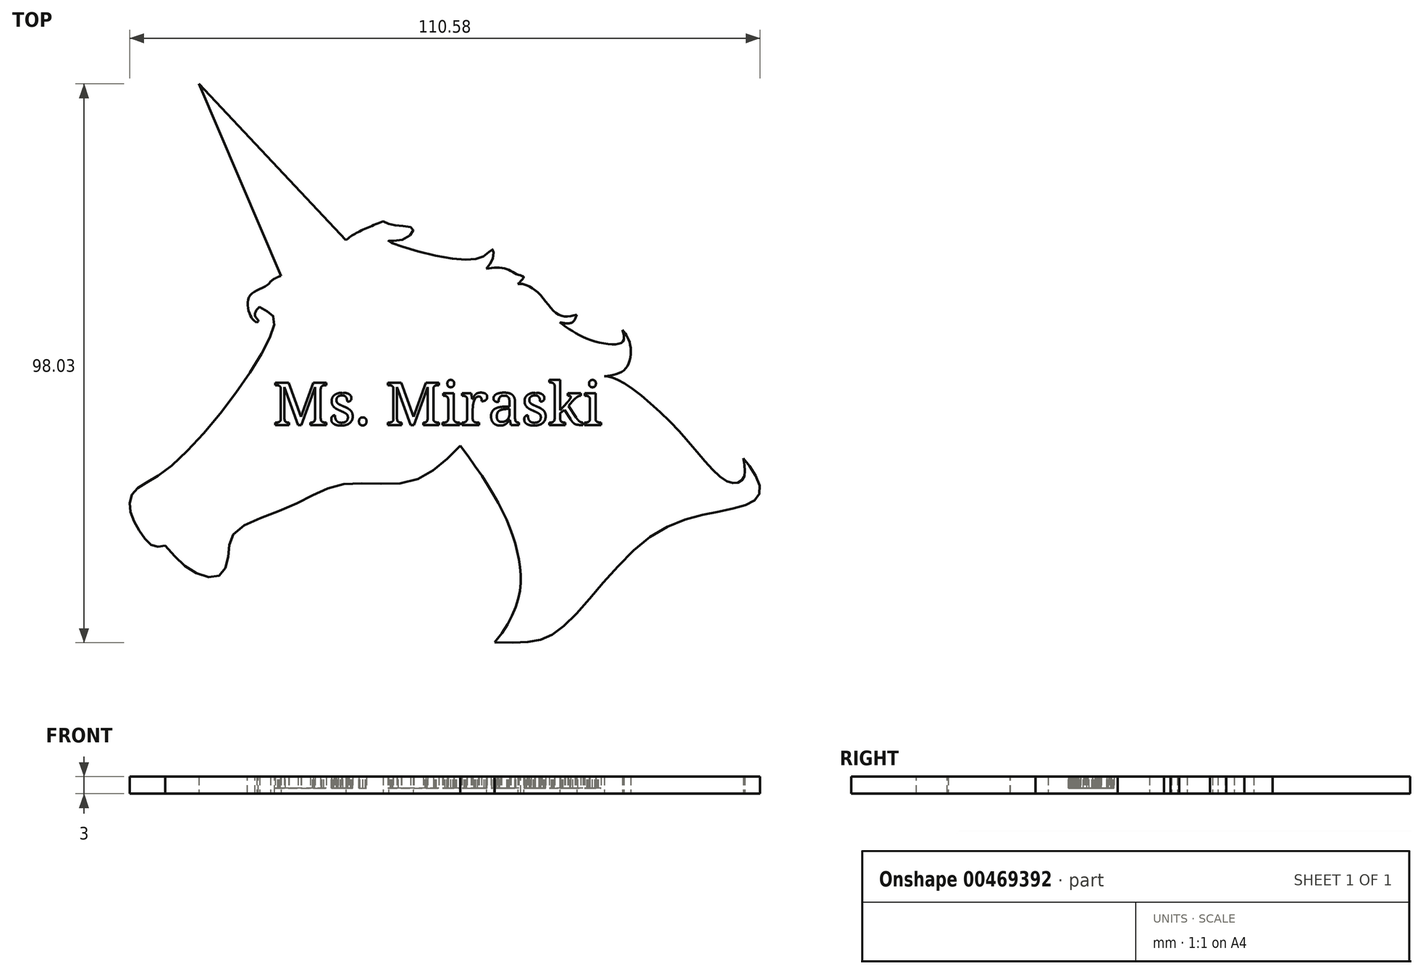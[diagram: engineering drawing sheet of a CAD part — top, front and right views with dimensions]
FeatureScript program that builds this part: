
annotation { "Feature Type Name" : "Feature", "Feature Type Description" : "" }
export const myFeature = defineFeature(function(context is Context, id is Id, definition is map)
    precondition{}
    {
        {
            var Q0;
            Q0=qCreatedBy(makeId("Top.planeOp"),FACE);
            var sketch = newSketch(context, id + "F0", { "sketchPlane" : qUnion([Q0])});
            skFitSpline(sketch, "E0", {"points": [v(22.82, -62.48) * mm, v(26.88, -47) * mm, v(16.78, -27.97) * mm], "startDerivative": vector(31.27, 37.7) * mm, "endDerivative": vector(-32.74, 43.32) * mm});
            skFitSpline(sketch, "E1", {"points": [v(16.78, -27.97) * mm, v(8.01, -34.25) * mm, v(-3.9, -34.75) * mm, v(-12.84, -38.56) * mm, v(-22.77, -43.2) * mm, v(-23.93, -47.5) * mm, v(-25.58, -50.8) * mm, v(-30.22, -49.98) * mm, v(-35, -45.51) * mm], "startDerivative": vector(-52.72, -53.92) * mm, "endDerivative": vector(-37.54, 43.37) * mm});
            skFitSpline(sketch, "E2", {"points": [v(-35, -45.51) * mm, v(-37.15, -45.51) * mm, v(-39.5, -42.86) * mm, v(-41.18, -38.88) * mm, v(-40.37, -35.9) * mm, v(-35, -32.4) * mm, v(-19.32, -13.9) * mm, v(-16.02, -5.26) * mm, v(-18.41, -3.62) * mm], "startDerivative": vector(-29.2, -5.84) * mm, "endDerivative": vector(-28.5, 26.2) * mm});
            skFitSpline(sketch, "E3", {"points": [v(-18.41, -3.62) * mm, v(-19.15, -5.35) * mm, v(-18.9, -6.38) * mm], "startDerivative": vector(-2.67, -1.56) * mm, "endDerivative": vector(-4.2, -2.33) * mm});
            skFitSpline(sketch, "E4", {"points": [v(-18.9, -6.38) * mm, v(-19.94, -5.35) * mm, v(-20.15, -1.67) * mm, v(-16.48, 0.83) * mm, v(-18.3, 7.27) * mm, v(-22.07, 18.67) * mm], "startDerivative": vector(-12.98, 8.34) * mm, "endDerivative": vector(-36.84, 54.57) * mm});
            skFitSpline(sketch, "E5", {"points": [v(-16.48, 0.83) * mm, v(-14.68, 1.83) * mm, v(-11.75, 2.52) * mm], "startDerivative": vector(2.86, 2.81) * mm, "endDerivative": vector(5.74, 0.86) * mm});
            skFitSpline(sketch, "E6", {"points": [v(22.82, -62.48) * mm, v(34.3, -60.16) * mm, v(51.24, -43.2) * mm, v(66.6, -38.47) * mm, v(69.36, -35.6) * mm, v(66.44, -30.2) * mm], "startDerivative": vector(81.23, -1.24) * mm, "endDerivative": vector(-22.09, 25.06) * mm});
            skFitSpline(sketch, "E7", {"points": [v(-22.07, 18.67) * mm, v(-15.16, 9.28) * mm, v(-11.75, 2.52) * mm], "startDerivative": vector(12.69, -12.67) * mm, "endDerivative": vector(6.1, -14.44) * mm});
            skFitSpline(sketch, "E8", {"points": [v(66.44, -30.2) * mm, v(66.44, -33.72) * mm, v(64.08, -34.43) * mm, v(54.6, -24.82) * mm, v(44.2, -16.3) * mm, v(42.07, -15.78) * mm], "startDerivative": vector(4.71, -26.28) * mm, "endDerivative": vector(-14.88, 1.16) * mm});
            skFitSpline(sketch, "E9", {"points": [v(42.07, -15.78) * mm, v(45.78, -14.44) * mm, v(46.57, -10.17) * mm, v(45.22, -7.63) * mm], "startDerivative": vector(12.55, 1.58) * mm, "endDerivative": vector(-5.67, 7.39) * mm});
            skFitSpline(sketch, "E10", {"points": [v(45.22, -7.63) * mm, v(45.22, -9.79) * mm, v(39.76, -9.48) * mm, v(34.24, -6.34) * mm], "startDerivative": vector(3.12, -11.04) * mm, "endDerivative": vector(-12.33, 9) * mm});
            skFitSpline(sketch, "E11", {"points": [v(34.24, -6.34) * mm, v(36.37, -6.34) * mm, v(37.22, -4.99) * mm], "startDerivative": vector(4.56, -0.78) * mm, "endDerivative": vector(1.33, 3.6) * mm});
            skFitSpline(sketch, "E12", {"points": [v(37.22, -4.99) * mm, v(33.99, -4.99) * mm, v(30.48, -1.17) * mm, v(27.78, 0.38) * mm, v(26.85, 0.41) * mm], "startDerivative": vector(-12.73, -3) * mm, "endDerivative": vector(-5.77, -0.46) * mm});
            skFitSpline(sketch, "E13", {"points": [v(26.85, 0.41) * mm, v(27.89, 1.62) * mm, v(26.85, 2.07) * mm, v(24.6, 3.13) * mm, v(21.35, 3.1) * mm], "startDerivative": vector(7.47, 6.51) * mm, "endDerivative": vector(-10.9, -1.43) * mm});
            skFitSpline(sketch, "E14", {"points": [v(21.35, 3.1) * mm, v(22.5, 4.93) * mm, v(22.5, 6.44) * mm, v(21.35, 5.58) * mm, v(15.37, 4.83) * mm, v(4.18, 7.9) * mm, v(6.77, 8.22) * mm, v(8.51, 10.07) * mm, v(5.6, 10.64) * mm, v(3.28, 11.38) * mm], "startDerivative": vector(15.37, 17.9) * mm, "endDerivative": vector(-20.5, 9.6) * mm});
            skFitSpline(sketch, "E15", {"points": [v(3.28, 11.38) * mm, v(-3.27, 8.07) * mm, v(-5.74, 5.03) * mm, v(-11.75, 2.52) * mm], "startDerivative": vector(-20.59, -7.89) * mm, "endDerivative": vector(-19.94, -5.81) * mm});
            skLineSegment(sketch, "E16", {"start": v(-14.68, 1.83) * mm, "end": v(-29.07, 35.51) * mm});
            skLineSegment(sketch, "E17", {"start": v(-29.07, 35.51) * mm, "end": v(-3.27, 8.07) * mm});
            skSolve(sketch);
        }
        {
            var Q0;
            Q0=makeQuery(id+"F0.imprint","IMPRINT",FACE,{"disambiguationData":[TD([[makeQuery(id+"F0.imprint","IMPRINT",EDGE,{"derivedFrom":sQuery(id+"F0.wireOp",EDGE,"E0")}),-1.0]])]});
            var Q1;
            {var subQ5=sQuery(id+"F0.wireOp",EDGE,"E17");Q1=makeQuery(id+"F0.imprint","IMPRINT",FACE,{"disambiguationData":[TD([[makeQuery(id+"F0.imprint","IMPRINT",EDGE,{"derivedFrom":subQ5}),-1.0]])]});}
            var Q2;
            {var subQ0=sQuery(id+"F0.wireOp",EDGE,"E16");var subQ3=sQuery(id+"F0.wireOp",EDGE,"E4");var subQ4=makeQuery(id+"F0.imprint","INTERSECT",VERTEX,{"disambiguationData":[OD(0.0)],"derivedFrom":[subQ3,subQ0]});Q2=makeQuery(id+"F0.imprint","IMPRINT",FACE,{"disambiguationData":[TD([[makeQuery(id+"F0.imprint","IMPRINT",EDGE,{"disambiguationData":[TD([[subQ4,-1.0]])],"derivedFrom":subQ3}),-1.0]])]});}
            var Q3;
            {var subQ0=sQuery(id+"F0.wireOp",EDGE,"E16");var subQ1=sQuery(id+"F0.wireOp",EDGE,"E4");var subQ2=makeQuery(id+"F0.imprint","INTERSECT",VERTEX,{"disambiguationData":[OD(0.0)],"derivedFrom":[subQ1,subQ0]});Q3=makeQuery(id+"F0.imprint","IMPRINT",FACE,{"disambiguationData":[TD([[makeQuery(id+"F0.imprint","IMPRINT",EDGE,{"disambiguationData":[TD([[subQ2,-1.0]])],"derivedFrom":subQ1}),1.0]])]});}
            extrude(context, id + "F1", {"entities" : qUnion([Q0, Q1, Q2, Q3]), "depth" : 3 * mm});
        }
        {
            var Q0;
            Q0=makeQuery(id+"F1.opExtrude","CAP_FACE",FACE,{"disambiguationData":[OSD([sQuery(id+"F0.wireOp",EDGE,"E0"),sQuery(id+"F0.wireOp",EDGE,"E1"),sQuery(id+"F0.wireOp",EDGE,"E2"),sQuery(id+"F0.wireOp",EDGE,"E3"),sQuery(id+"F0.wireOp",EDGE,"E4"),sQuery(id+"F0.wireOp",EDGE,"E5"),sQuery(id+"F0.wireOp",EDGE,"E6"),sQuery(id+"F0.wireOp",EDGE,"E8"),sQuery(id+"F0.wireOp",EDGE,"E9"),sQuery(id+"F0.wireOp",EDGE,"E10"),sQuery(id+"F0.wireOp",EDGE,"E11"),sQuery(id+"F0.wireOp",EDGE,"E12"),sQuery(id+"F0.wireOp",EDGE,"E13"),sQuery(id+"F0.wireOp",EDGE,"E14"),sQuery(id+"F0.wireOp",EDGE,"E15"),sQuery(id+"F0.wireOp",EDGE,"E16"),sQuery(id+"F0.wireOp",EDGE,"E17")])],"isStart":false});
            var sketch = newSketch(context, id + "F2", { "sketchPlane" : qUnion([Q0])});
            skText(sketch, "E18", { "text": "Ms. Miraski", "fontName": "NotoSerif-Regular.ttf"});
            const initialGuessF2  = {"E18": [-0.01608, -0.02434, 1, 0, 0.00749]};
            skSetInitialGuess(sketch, initialGuessF2);
            skSolve(sketch);
        }
        {
            var Q0;
            Q0=makeQuery(id+"F2.imprint","IMPRINT",FACE,{"disambiguationData":[TD([[makeQuery(id+"F2.imprint","IMPRINT",EDGE,{"derivedFrom":sQuery(id+"F2.wireOp",EDGE,"E18.sketch_text.stroke-0")}),1.0]])]});
            var Q1;
            Q1=makeQuery(id+"F2.imprint","IMPRINT",FACE,{"disambiguationData":[TD([[makeQuery(id+"F2.imprint","IMPRINT",EDGE,{"derivedFrom":sQuery(id+"F2.wireOp",EDGE,"E18.sketch_text.stroke-246")}),1.0]])]});
            extrude(context, id + "F3", {"entities" : qUnion([Q0, Q1]), "operationType" : NewBodyOperationType.ADD, "depth" : 2 * mm});
        }
        {
            var Q0;
            Q0=makeQuery(id+"F1.opExtrude","CAP_FACE",FACE,{"disambiguationData":[OSD([sQuery(id+"F0.wireOp",EDGE,"E0"),sQuery(id+"F0.wireOp",EDGE,"E1"),sQuery(id+"F0.wireOp",EDGE,"E2"),sQuery(id+"F0.wireOp",EDGE,"E3"),sQuery(id+"F0.wireOp",EDGE,"E4"),sQuery(id+"F0.wireOp",EDGE,"E5"),sQuery(id+"F0.wireOp",EDGE,"E6"),sQuery(id+"F0.wireOp",EDGE,"E8"),sQuery(id+"F0.wireOp",EDGE,"E9"),sQuery(id+"F0.wireOp",EDGE,"E10"),sQuery(id+"F0.wireOp",EDGE,"E11"),sQuery(id+"F0.wireOp",EDGE,"E12"),sQuery(id+"F0.wireOp",EDGE,"E13"),sQuery(id+"F0.wireOp",EDGE,"E14"),sQuery(id+"F0.wireOp",EDGE,"E15"),sQuery(id+"F0.wireOp",EDGE,"E16"),sQuery(id+"F0.wireOp",EDGE,"E17")])],"isStart":true});
            extrude(context, id + "F4", {"entities" : qUnion([Q0]), "operationType" : NewBodyOperationType.REMOVE, "oppositeDirection" : true, "depth" : 2 * mm});
        }
    });
